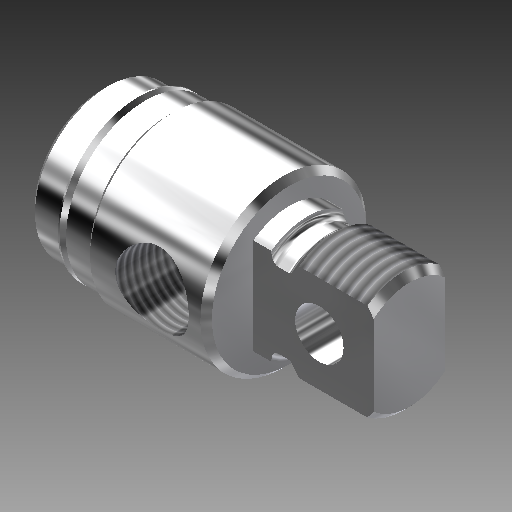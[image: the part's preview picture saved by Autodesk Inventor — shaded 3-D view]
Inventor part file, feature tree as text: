
AUTODESK INVENTOR PART (.ipt)
format: ipt  version: 2017 (Build 210142000, 142)  size: 382,464 bytes
history: native  units: in
note: dims shown in document units (in); Inventor stores cm internally (conversion verified against a paired STEP export)
features: other x154, sketch x7, revolve x4, thread x2, extrude x2, hole x1
ambient origin geometry x8: Origin, YZ Plane, XZ Plane, XY Plane, X Axis, Y Axis, Z Axis, Center Point
bodies: Solid1 (feature_tree)
feature tree (170):
  revolve  "Revolution1"  Angle=360.0deg
  revolve  "Revolution2"  [1 undecoded]
  thread  "Thread1"  [1 undecoded]
  extrude  "Extrusion1"  TaperAngle=360.0deg  [1 undecoded]
  hole  "Hole1"  [1 undecoded]
  revolve  "Revolution3"  [1 undecoded]
  thread  "Thread2"  [1 undecoded]
  revolve  "Revolution4"  [1 undecoded]
  extrude  "Extrusion2"  [1 undecoded]
  other  "1_XY"
  other  "1_YZ"
  other  "1_ZX"
  other  "1_X"
  other  "1_Y"
  other  "1_Z"
  other  "1_Center"
  other  "c1_XY"
  other  "c1_YZ"
  other  "c1_ZX"
  other  "c1_X"
  other  "c1_Y"
  other  "c1_Z"
  other  "c1_Center"
  other  "c2_XY"
  other  "c2_YZ"
  other  "c2_ZX"
  other  "c2_X"
  other  "c2_Y"
  other  "c2_Z"
  other  "c2_Center"
  other  "cc1_XY"
  other  "cc1_YZ"
  other  "cc1_ZX"
  other  "cc1_X"
  other  "cc1_Y"
  other  "cc1_Z"
  other  "cc1_Center"
  other  "cc2_XY"
  other  "cc2_YZ"
  other  "cc2_ZX"
  other  "cc2_X"
  other  "cc2_Y"
  other  "cc2_Z"
  other  "cc2_Center"
  other  "lovra1_XY"
  other  "lovra1_YZ"
  other  "lovra1_ZX"
  other  "lovra1_X"
  other  "lovra1_Y"
  other  "lovra1_Z"
  other  "lovra1_Center"
  other  "lovra2_XY"
  other  "lovra2_YZ"
  other  "lovra2_ZX"
  other  "lovra2_X"
  other  "lovra2_Y"
  other  "lovra2_Z"
  other  "lovra2_Center"
  other  "lovra21_XY"
  other  "lovra21_YZ"
  other  "lovra21_ZX"
  other  "lovra21_X"
  other  "lovra21_Y"
  other  "lovra21_Z"
  other  "lovra21_Center"
  other  "lovra22_XY"
  other  "lovra22_YZ"
  other  "lovra22_ZX"
  other  "lovra22_X"
  other  "lovra22_Y"
  other  "lovra22_Z"
  other  "lovra22_Center"
  other  "lovra3_XY"
  other  "lovra3_YZ"
  other  "lovra3_ZX"
  other  "lovra3_X"
  other  "lovra3_Y"
  other  "lovra3_Z"
  other  "lovra3_Center"
  other  "olen_XY"
  other  "olen_YZ"
  other  "olen_ZX"
  other  "olen_X"
  other  "olen_Y"
  other  "olen_Z"
  other  "olen_Center"
  other  "p1_XY"
  other  "p1_YZ"
  other  "p1_ZX"
  other  "p1_X"
  other  "p1_Y"
  other  "p1_Z"
  other  "p1_Center"
  other  "p2_XY"
  other  "p2_YZ"
  other  "p2_ZX"
  other  "p2_X"
  other  "p2_Y"
  other  "p2_Z"
  other  "p2_Center"
  other  "port_XY"
  other  "port_YZ"
  other  "port_ZX"
  other  "port_X"
  other  "port_Y"
  other  "port_Z"
  other  "port_Center"
  other  "port2_XY"
  other  "port2_YZ"
  other  "port2_ZX"
  other  "port2_X"
  other  "port2_Y"
  other  "port2_Z"
  other  "port2_Center"
  other  "thd1_XY"
  other  "thd1_YZ"
  other  "thd1_ZX"
  other  "thd1_X"
  other  "thd1_Y"
  other  "thd1_Z"
  other  "thd1_Center"
  other  "thd2_XY"
  other  "thd2_YZ"
  other  "thd2_ZX"
  other  "thd2_X"
  other  "thd2_Y"
  other  "thd2_Z"
  other  "thd2_Center"
  other  "to_mounting_bracket_XY"
  other  "to_mounting_bracket_YZ"
  other  "to_mounting_bracket_ZX"
  other  "to_mounting_bracket_X"
  other  "to_mounting_bracket_Y"
  other  "to_mounting_bracket_Z"
  other  "to_mounting_bracket_Center"
  other  "to_nut_XY"
  other  "to_nut_YZ"
  other  "to_nut_ZX"
  other  "to_nut_X"
  other  "to_nut_Y"
  other  "to_nut_Z"
  other  "to_nut_Center"
  other  "to_pin_XY"
  other  "to_pin_YZ"
  other  "to_pin_ZX"
  other  "to_pin_X"
  other  "to_pin_Y"
  other  "to_pin_Z"
  other  "to_pin_Center"
  other  "to_screw_XY"
  other  "to_screw_YZ"
  other  "to_screw_ZX"
  other  "to_screw_X"
  other  "to_screw_Y"
  other  "to_screw_Z"
  other  "to_screw_Center"
  other  "to_tube_XY"
  other  "to_tube_YZ"
  other  "to_tube_ZX"
  other  "to_tube_X"
  other  "to_tube_Y"
  other  "to_tube_Z"
  other  "to_tube_Center"
  sketch  "Sketch_8"  dims[d2=0.3547in d3=0.0in d4=0.625in d5=0.0in]
  sketch  "Sketch_15"  dims[d14=0.3021in d15=0.0in d16=360.0deg]
  sketch  "Sketch_9"  dims[d6=0.312in d7=0.75in d8=0.375in d9=0.25in d10=0.5635in d11=0.9284in d12=120.0deg d13=360.0deg]
  sketch  "Sketch4"  dims[d0=360.0deg d1=360.0deg]
  sketch  "Sketch_68"
  sketch  "Sketch_24"  dims[d17=0.5587in d18=0.0in d19=0.0in d20=0.0in d21=0.0in d22=0.0in]
  sketch  "Sketch_43"
note: 8 required parameter values undecoded (feature->parameter linkage not recoverable at this tier; creation-order binding heuristic only, values carry confidence <= 0.55)